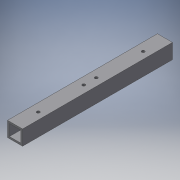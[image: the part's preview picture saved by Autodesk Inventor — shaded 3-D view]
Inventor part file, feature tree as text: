
AUTODESK INVENTOR PART (.ipt)
format: ipt  version: 2018 (Build 220112000, 112)  size: 153,088 bytes
history: native  units: in
note: dims shown in document units (in); Inventor stores cm internally (conversion verified against a paired STEP export)
features: extrude x5, sketch x5, projected_geometry x2
ambient origin geometry x8: Origin, YZ Plane, XZ Plane, XY Plane, X Axis, Y Axis, Z Axis, Center Point
bodies: Solid1 (feature_tree)
feature tree (12):
  extrude  "Extrusion1"  Depth=1.0in
  extrude  "Extrusion2"  Depth=0.125in TaperAngle=0.0deg
  extrude  "Extrusion3"  Depth=0.5in
  extrude  "Extrusion4"  Depth=0.2031in
  extrude  "Extrusion5"  Depth=1.0in TaperAngle=0.0deg
  sketch  "Sketch1"  dims[d0=1.0in d1=1.0in]
  sketch  "Sketch2"  dims[d2=0.125in d3=7.5in d4=0.0in]
  sketch  "Sketch3"  dims[d6=0.5in d7=0.5in]
  projected_geometry  "Projected Loop1"
  sketch  "Sketch4"  dims[d8=0.2031in d9=0.2031in]
  projected_geometry  "Projected Loop2"
  sketch  "Sketch5"  dims[d10=6.0in d11=0.0in d12=0.5in d13=0.0in d14=1.0in d15=0.0in d16=1.0in d17=0.0in d18=4.585in d19=4.585in d20=0.2031in d21=0.2031in d22=2.0in d23=0.0in]
